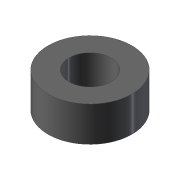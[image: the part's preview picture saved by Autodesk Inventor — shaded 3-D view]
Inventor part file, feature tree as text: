
AUTODESK INVENTOR PART (.ipt)
format: ipt  version: 2020 (Build 240168000, 168)  size: 86,528 bytes
history: native  units: mm
features: extrude x1, sketch x1
ambient origin geometry x8: Origin, YZ Plane, XZ Plane, XY Plane, X Axis, Y Axis, Z Axis, Center Point
bodies: Solid1 (feature_tree)
feature tree (2):
  extrude  "Extrusion1"  Depth=5.0mm
  sketch  "Sketch1"  dims[d0=6.0mm d1=12.0mm d2=5.0mm d3=0.0mm]
